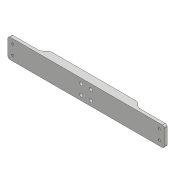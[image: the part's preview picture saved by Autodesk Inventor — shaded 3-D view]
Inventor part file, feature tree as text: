
AUTODESK INVENTOR PART (.ipt)
format: ipt  version: 2018 (Build 220112000, 112)  size: 159,744 bytes
history: native  units: mm
features: sketch x4, extrude x3, fillet x3, hole x2, projected_geometry x2, chamfer x1, mirror x1
ambient origin geometry x8: Origin, YZ Plane, XZ Plane, XY Plane, X Axis, Y Axis, Z Axis, Center Point
bodies: Solid1 (feature_tree)
feature tree (16):
  extrude  "Extrusion1"  Depth=160.0mm
  sketch  "Sketch2"  dims[d6=3.0mm d7=0.0mm d8=14.0mm]
  hole  "Hole1"  [1 undecoded]
  extrude  "Extrusion2"  Depth=9.899495mm
  hole  "Hole2"  [1 undecoded]
  fillet  "Fillet1"  Radius=2.0mm
  extrude  "Extrusion3"  Depth=10.0mm
  chamfer  "Chamfer1"  Distance=150.0mm
  fillet  "Fillet2"  Radius=2.0mm
  fillet  "Fillet3"  Radius=100.0mm
  mirror  "Mirror1"
  sketch  "Sketch1"  dims[d0=20.0mm d1=160.0mm]
  projected_geometry  "Projected Loop1"
  sketch  "Sketch3"  dims[d9=9.899495mm d10=9.899495mm]
  sketch  "Sketch4"  dims[d12=3.4mm d13=6.0mm d14=6.3mm d15=2.0mm d16=90.0deg d17=8.0mm d18=20.594885mm d19=6.0mm d20=2.0mm d21=0.0mm d22=10.0mm d23=150.0mm d24=2.459mm d25=6.0mm d26=6.3mm d27=2.0mm d28=90.0deg d29=8.8mm d30=20.594885mm d31=2.0mm d32=100.0mm d33=5.0mm d34=1.5mm d35=0.0mm d36=5.0mm d37=2.0mm d38=45.0deg d39=5.0mm d40=1.0mm]
  projected_geometry  "Projected Loop2"
note: 2 required parameter values undecoded (feature->parameter linkage not recoverable at this tier; creation-order binding heuristic only, values carry confidence <= 0.55)
